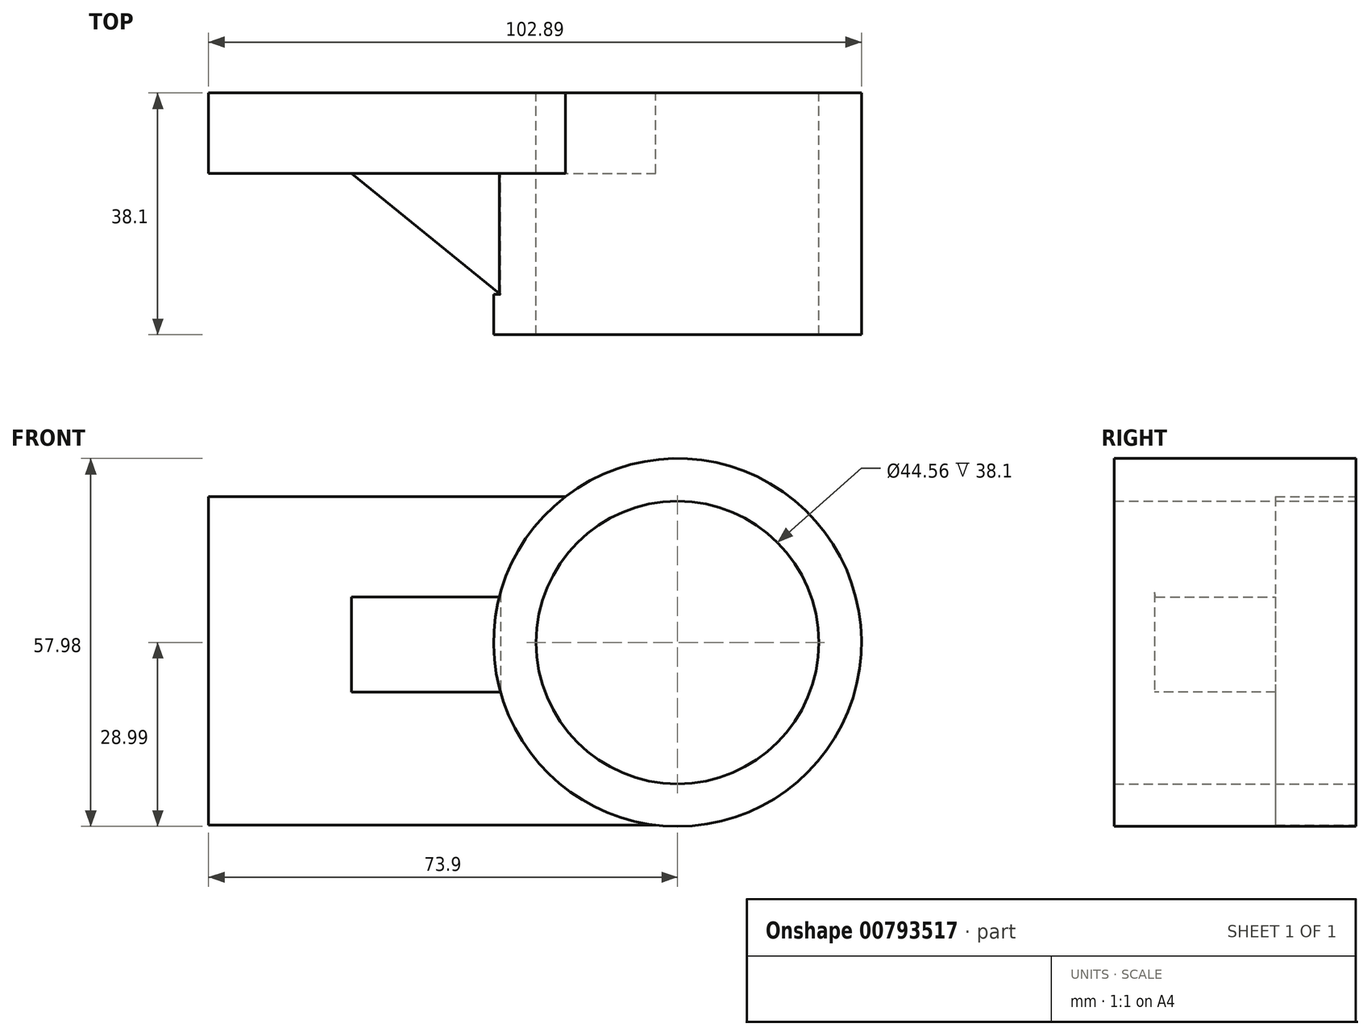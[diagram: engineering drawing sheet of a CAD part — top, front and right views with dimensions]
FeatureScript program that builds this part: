
annotation { "Feature Type Name" : "Feature", "Feature Type Description" : "" }
export const myFeature = defineFeature(function(context is Context, id is Id, definition is map)
    precondition{}
    {
        {
            var Q0;
            Q0=qCreatedBy(makeId("Front.planeOp"),FACE);
            var sketch = newSketch(context, id + "F0", { "sketchPlane" : qUnion([Q0])});
            skCircle(sketch, "E0", {"center": v(0, 0) * mm, "radius": 22.28 * mm});
            skCircle(sketch, "E1", {"center": v(0, 0) * mm, "radius": 28.99 * mm});
            skLineSegment(sketch, "E2", {"start": v(-17.7, 22.96) * mm, "end": v(-73.9, 22.96) * mm});
            skLineSegment(sketch, "E3", {"start": v(-73.9, 22.96) * mm, "end": v(-73.9, -28.79) * mm});
            skLineSegment(sketch, "E4", {"start": v(-73.9, -28.79) * mm, "end": v(-3.42, -28.79) * mm});
            skSolve(sketch);
        }
        {
            var Q0;
            Q0=makeQuery(id+"F0.imprint","IMPRINT",FACE,{"disambiguationData":[TD([[makeQuery(id+"F0.imprint","IMPRINT",EDGE,{"derivedFrom":sQuery(id+"F0.wireOp",EDGE,"E0")}),-1.0]])]});
            extrude(context, id + "F1", {"entities" : qUnion([Q0]), "depth" : 38.1 * mm, "offsetDistance" : 25.4 * mm});
        }
        {
            var Q0;
            {var subQ0=sQuery(id+"F0.wireOp",EDGE,"E2");Q0=makeQuery(id+"F0.imprint","IMPRINT",FACE,{"disambiguationData":[TD([[makeQuery(id+"F0.imprint","IMPRINT",EDGE,{"derivedFrom":subQ0}),1.0]])]});}
            extrude(context, id + "F2", {"entities" : qUnion([Q0]), "operationType" : NewBodyOperationType.ADD, "depth" : 12.7 * mm, "offsetDistance" : 25.4 * mm});
        }
        {
            var Q0;
            Q0=makeQuery(id+"F2.opExtrude","CAP_FACE",FACE,{"disambiguationData":[OSD([sQuery(id+"F0.wireOp",EDGE,"E1"),sQuery(id+"F0.wireOp",EDGE,"E2"),sQuery(id+"F0.wireOp",EDGE,"E3"),sQuery(id+"F0.wireOp",EDGE,"E4")])],"isStart":false});
            var sketch = newSketch(context, id + "F3", { "sketchPlane" : qUnion([Q0])});
            skLineSegment(sketch, "E5", {"start": v(-28.1, 7.16) * mm, "end": v(-51.4, 7.16) * mm});
            skLineSegment(sketch, "E6", {"start": v(-51.4, 7.16) * mm, "end": v(-51.4, -7.84) * mm});
            skLineSegment(sketch, "E7", {"start": v(-51.4, -7.84) * mm, "end": v(-27.9, -7.84) * mm});
            skSolve(sketch);
        }
        {
            var Q0;
            {var subQ0=sQuery(id+"F3.wireOp",EDGE,"E5");Q0=makeQuery(id+"F3.imprint","IMPRINT",FACE,{"disambiguationData":[TD([[makeQuery(id+"F3.imprint","IMPRINT",EDGE,{"derivedFrom":subQ0}),1.0]])]});}
            extrude(context, id + "F4", {"entities" : qUnion([Q0]), "operationType" : NewBodyOperationType.ADD, "depth" : 19.05 * mm, "offsetDistance" : 25.4 * mm});
        }
        {
            var Q0;
            Q0=makeQuery(id+"F4.opExtrude","SWEPT_FACE",FACE,{"disambiguationData":[OSD([sQuery(id+"F3.wireOp",EDGE,"E7")])]});
            var sketch = newSketch(context, id + "F5", { "sketchPlane" : qUnion([Q0])});
            skLineSegment(sketch, "E8", {"start": v(-51.4, 12.7) * mm, "end": v(-27.9, 31.75) * mm});
            skSolve(sketch);
        }
        {
            var Q0;
            Q0=makeQuery(id+"F5.imprint","IMPRINT",FACE,{"disambiguationData":[TD([[makeQuery(id+"F5.imprint","IMPRINT",EDGE,{"derivedFrom":sQuery(id+"F5.wireOp",EDGE,"E8")}),1.0]])]});
            extrude(context, id + "F6", {"entities" : qUnion([Q0]), "operationType" : NewBodyOperationType.REMOVE, "oppositeDirection" : true, "depth" : 25.4 * mm, "offsetDistance" : 25.4 * mm});
        }
    });
